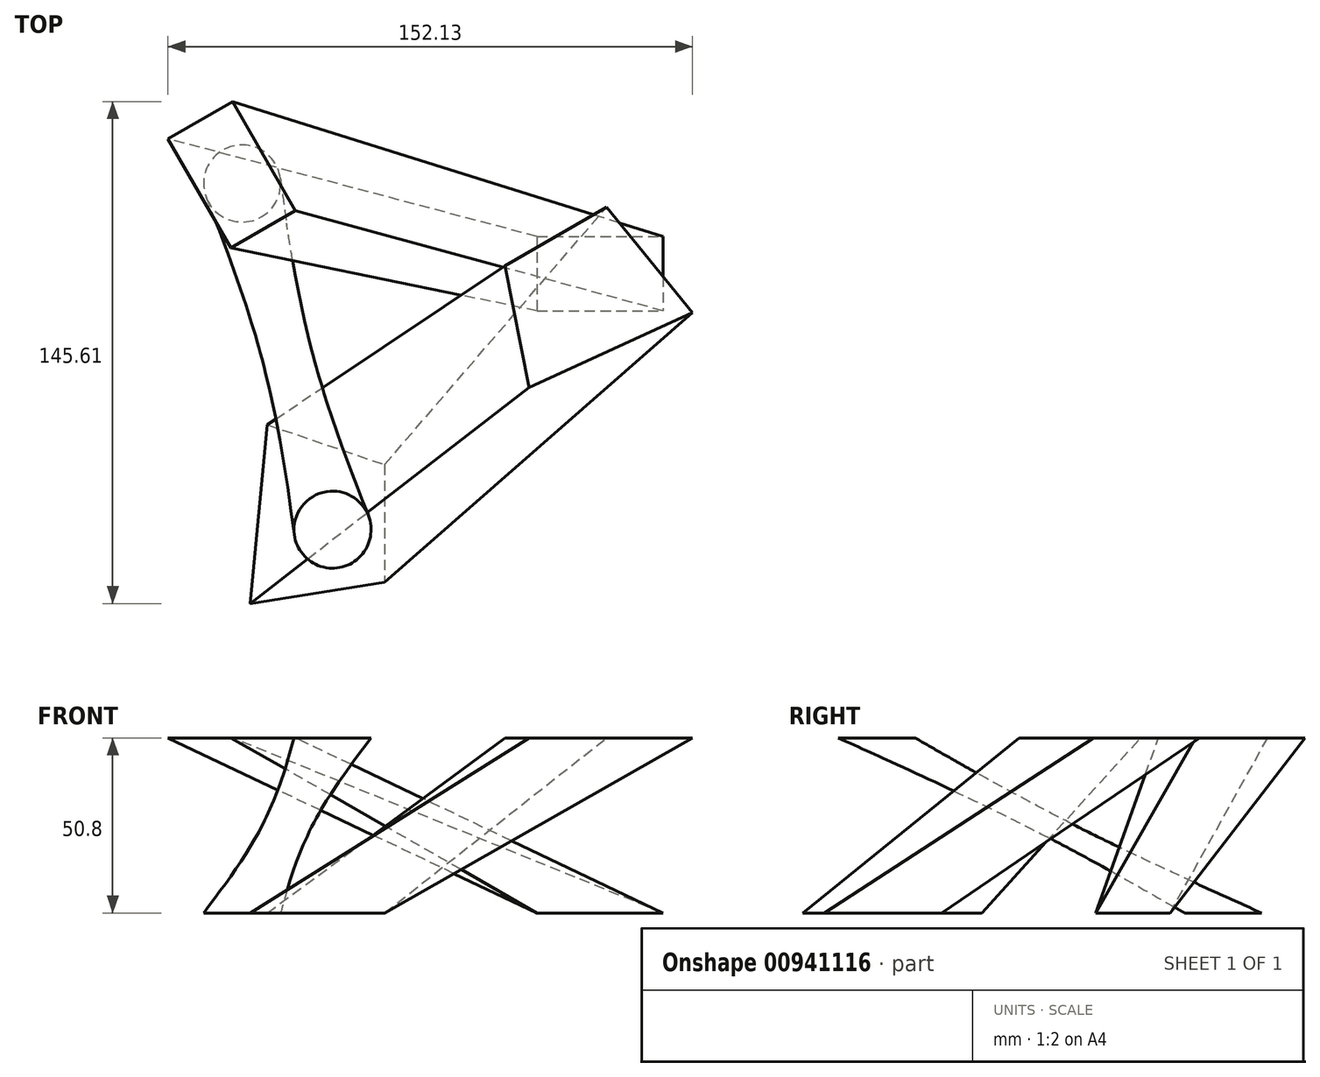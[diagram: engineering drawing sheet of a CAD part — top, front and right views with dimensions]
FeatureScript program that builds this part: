
annotation { "Feature Type Name" : "Feature", "Feature Type Description" : "" }
export const myFeature = defineFeature(function(context is Context, id is Id, definition is map)
    precondition{}
    {
        {
            var Q0;
            Q0=qCreatedBy(makeId("Top.planeOp"),FACE);
            var sketch = newSketch(context, id + "F0", { "sketchPlane" : qUnion([Q0])});
            skCircle(sketch, "E0", {"center": v(-62.28, 52.52) * mm, "radius": 11.18 * mm});
            skLineSegment(sketch, "E1.bottom", {"start": v(23.25, 37.16) * mm, "end": v(59.79, 37.16) * mm});
            skLineSegment(sketch, "E1.top", {"start": v(23.25, 15.57) * mm, "end": v(59.79, 15.57) * mm});
            skLineSegment(sketch, "E1.left", {"start": v(23.25, 37.16) * mm, "end": v(23.25, 15.57) * mm});
            skLineSegment(sketch, "E1.right", {"start": v(59.79, 37.16) * mm, "end": v(59.79, 15.57) * mm});
            skLineSegment(sketch, "E2", {"start": v(-55, -17.45) * mm, "end": v(-20.95, -29.08) * mm});
            skLineSegment(sketch, "E3", {"start": v(-20.95, -29.08) * mm, "end": v(-20.95, -63.13) * mm});
            skLineSegment(sketch, "E4", {"start": v(-20.95, -63.13) * mm, "end": v(-59.98, -69.35) * mm});
            skLineSegment(sketch, "E5", {"start": v(-59.98, -69.35) * mm, "end": v(-55, -17.45) * mm});
            skLineSegment(sketch, "E6", {"start": v(-82.91, 71.7) * mm, "end": v(-82.91, 30.26) * mm, "construction": true});
            skSolve(sketch);
        }
        {
            var Q0;
            Q0=qCreatedBy(makeId("Top.planeOp"),FACE);
            cPlane(context, id + "F1", {"entities" : qUnion([Q0]), "cplaneType" : CPlaneType.OFFSET, "offset" : 50.8 * mm, "width" : 152.4 * mm, "height" : 152.4 * mm});
        }
        {
            var Q0;
            Q0=qCreatedBy(id+"F1.planeOp",FACE);
            var sketch = newSketch(context, id + "F2", { "sketchPlane" : qUnion([Q0])});
            skCircle(sketch, "E7.0", {"center": v(-36.07, -47.94) * mm, "radius": 11.18 * mm});
            skLineSegment(sketch, "E7.1.0", {"start": v(-65.53, 33.82) * mm, "end": v(-46.83, 44.61) * mm});
            skLineSegment(sketch, "E7.1.1", {"start": v(-46.83, 44.61) * mm, "end": v(-65.1, 76.26) * mm});
            skLineSegment(sketch, "E7.1.2", {"start": v(-65.1, 76.26) * mm, "end": v(-83.8, 65.46) * mm});
            skLineSegment(sketch, "E7.1.3", {"start": v(-83.8, 65.46) * mm, "end": v(-65.53, 33.82) * mm});
            skLineSegment(sketch, "E7.2.0", {"start": v(20.9, -6.64) * mm, "end": v(68.33, 15) * mm});
            skLineSegment(sketch, "E7.2.1", {"start": v(68.33, 15) * mm, "end": v(43.42, 45.68) * mm});
            skLineSegment(sketch, "E7.2.2", {"start": v(43.42, 45.68) * mm, "end": v(13.94, 28.66) * mm});
            skLineSegment(sketch, "E7.2.3", {"start": v(13.94, 28.66) * mm, "end": v(20.9, -6.64) * mm});
            skSolve(sketch);
        }
        {
            var Q0;
            Q0=makeQuery(id+"F0.imprint","IMPRINT",FACE,{"disambiguationData":[TD([[makeQuery(id+"F0.imprint","IMPRINT",EDGE,{"derivedFrom":sQuery(id+"F0.wireOp",EDGE,"E0")}),1.0]])]});
            var Q1;
            Q1=makeQuery(id+"F2.imprint","IMPRINT",FACE,{"disambiguationData":[TD([[makeQuery(id+"F2.imprint","IMPRINT",EDGE,{"derivedFrom":sQuery(id+"F2.wireOp",EDGE,"E7.0")}),1.0]])]});
            loft(context, id + "F3", {"sheetProfilesArray" : [{ "sheetProfileEntities" : qUnion([Q0]) }, { "sheetProfileEntities" : qUnion([Q1]) }]});
        }
        {
            var Q0;
            Q0=makeQuery(id+"F0.imprint","IMPRINT",FACE,{"disambiguationData":[TD([[makeQuery(id+"F0.imprint","IMPRINT",EDGE,{"derivedFrom":sQuery(id+"F0.wireOp",EDGE,"E2")}),-1.0]])]});
            var Q1;
            Q1=makeQuery(id+"F2.imprint","IMPRINT",FACE,{"disambiguationData":[TD([[makeQuery(id+"F2.imprint","IMPRINT",EDGE,{"derivedFrom":sQuery(id+"F2.wireOp",EDGE,"E7.2.0")}),1.0]])]});
            loft(context, id + "F4", {"sheetProfilesArray" : [{ "sheetProfileEntities" : qUnion([Q0]) }, { "sheetProfileEntities" : qUnion([Q1]) }]});
        }
        {
            var Q0;
            Q0=makeQuery(id+"F0.imprint","IMPRINT",FACE,{"disambiguationData":[TD([[makeQuery(id+"F0.imprint","IMPRINT",EDGE,{"derivedFrom":sQuery(id+"F0.wireOp",EDGE,"E1.bottom")}),-1.0]])]});
            var Q1;
            Q1=makeQuery(id+"F2.imprint","IMPRINT",FACE,{"disambiguationData":[TD([[makeQuery(id+"F2.imprint","IMPRINT",EDGE,{"derivedFrom":sQuery(id+"F2.wireOp",EDGE,"E7.1.0")}),1.0]])]});
            loft(context, id + "F5", {"sheetProfilesArray" : [{ "sheetProfileEntities" : qUnion([Q0]) }, { "sheetProfileEntities" : qUnion([Q1]) }]});
        }
    });
